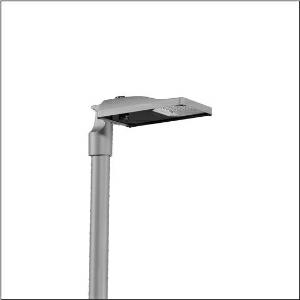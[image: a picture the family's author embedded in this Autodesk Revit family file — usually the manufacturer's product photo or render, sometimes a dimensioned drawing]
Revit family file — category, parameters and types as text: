
# Revit family: streetlight_sl_31_micro___st0_5a_5xh5b31t08ca_3c37
name_source: partatom
category: Lighting Fixtures
units: mm (PartAtom-declared; Revit-internal decimal feet)

## family parameters
Cut with Voids When Loaded = No
Host = Face
Light Source = No
Part Type = Normal
Room Calculation Point = No
Round Connector Dimension = Use Diameter
Shared = No

## types (1)
- --- (1 x LED, 1440 lm, 10.2 W, 3000K)
    Apparent Load = 10 VA
    CIE Flux Codes = 41 75 97 100 100
    Color Rendering = 70
    Color Temperature = 3000K
    Default Elevation = 1800 mm
    Description = Streetlight SL 31 micro D4i, Desk-Remote mast luminaire for post-top, side-entry; light control with lens of PMMA; light distribution: ST0.5a, direct asymmetric distribution, for standard-compliant lighting for roads and squares; LED: luminous flux: 1.440lm, light colour: 730, colour temperature: 3000K; luminous efficacy: 141,2lm/W; control: pre-setting: logarithmic dimming characteristic, flexible luminous flux parameterisation, time-dependent luminous flux control, constant luminous flux control, power reduction, intelligent temperature release in ECG and LED module, overheat protection; luminaire housing, of diecast aluminium, SITECO metallic grey (DB 702S), corrosivity category C5 high according to DIN EN ISO 12944; cover of toughened safety glass, transparent, opened without tools; mast flange of diecast aluminium, SITECO metallic grey (DB 702S), spigot size: 76/60mm, mast flange included unmounted; cable length: 5,5m, connection cable pre-assembled; mains connection: 220..240V, AC, 50/60Hz; power consumption (at start of service life): 10,2W / (at end of service life): 10,5W / (with reduced operation 50%): 5,3W; protection rating (complete): IP66; insulation class (complete): insulation class II (safety insulation); impact resistance: IK09; certification: CE, ENEC, ENEC+, VDE, UKCA, ZD4i; permissible operating ambient temperature for outdoor applications: -40..+50°C; packaging unit: 1 piece

Light Distribution: ST0.5a
    Height = 76 mm
    Lamp = 1 x LED
    Lamp Light Flux = 1440 lm
    Lamp Power = 10.2 W
    Lamp count = 1
    Length = 467 mm
    Luminous efficacy = 141 lm/W
    Manufacturer = Siteco
    ModVariant = No
    Model = 5XH5B31T08CA
    Number of Poles = 1
    OnlyDefault = Yes
    Power Factor = 1
    Product Name = Streetlight SL 31 micro | ST0.5a
    Product group = mast luminaire | pylon top
    ProductGroupID = 6100
    Protection Class = Protection class II
    Protection Degree = IP 66
    RLX_Detail_Level = 1
    RLX_Emergency_Light_Flux = 0 lm
    RLX_Emergency_Type = 0
    RLX_Emergency_Type_DB = No
    RlxData = <blob elided: 55117 chars, md5=eb89ab73>
    Socket = socket
    Standby Power = 0 W
    System Light Flux = 1440 lm
    System Power = 10 W
    Type Comments = factory setting: luminous flux: 100 % | dim-lin: 254 | 386 mA
    Type Image = l_1300315.jpg
    URL = http://relux.com
    VarID = @adj_055619
    Voltage = 0 V
    Weight = 0.00 kg
    Width = 265 mm

## geometry (parser evidence)
native form markers: Blend x4, Sweep x10
no freeform markers — native parametric forms only
